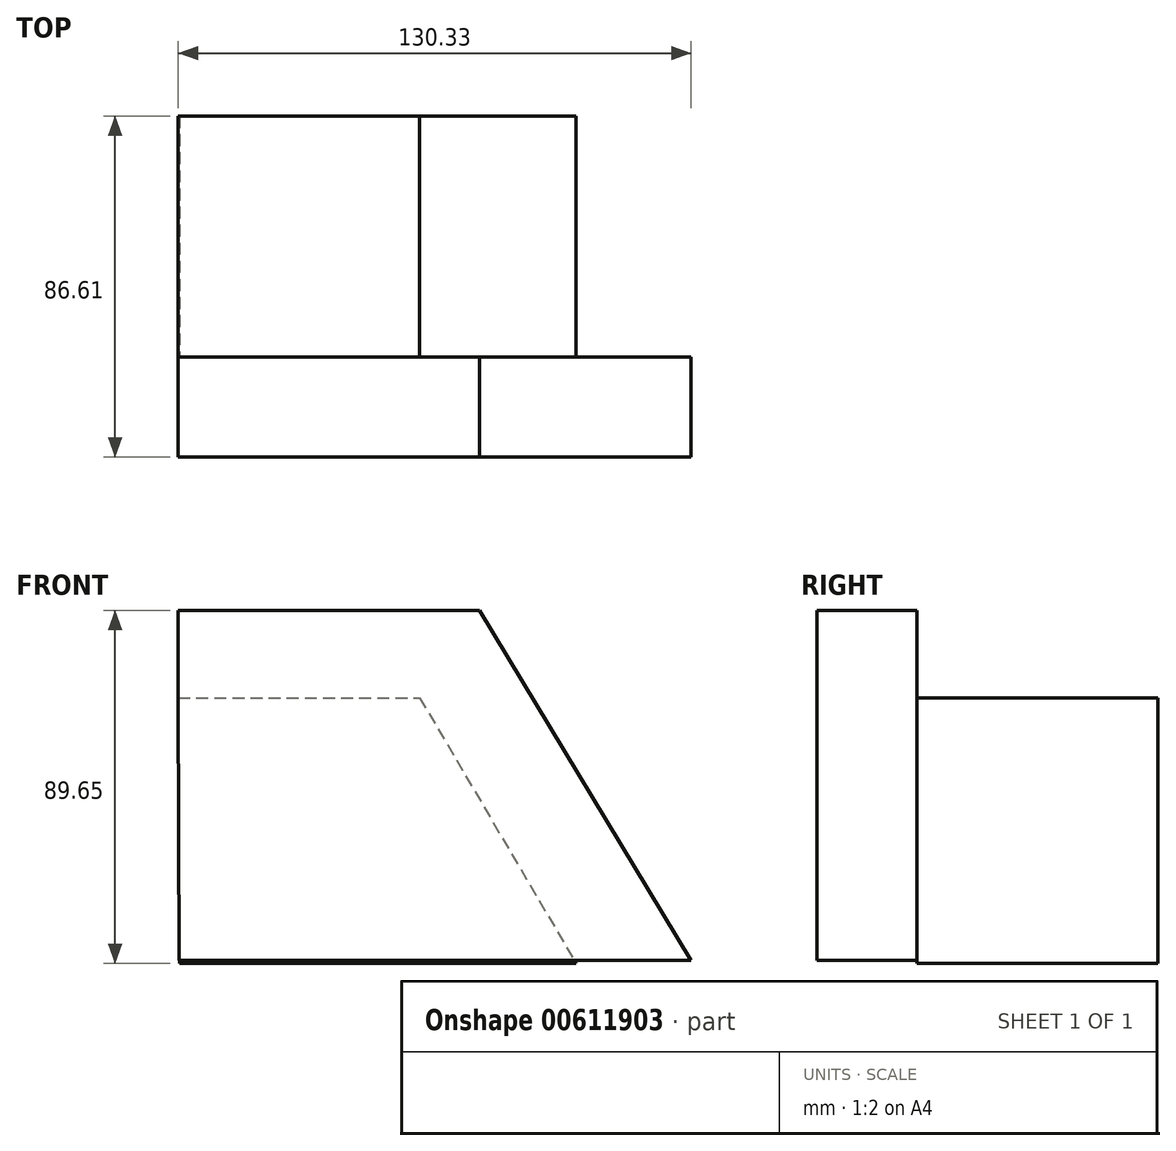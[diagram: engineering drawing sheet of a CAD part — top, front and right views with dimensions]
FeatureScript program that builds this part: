
annotation { "Feature Type Name" : "Feature", "Feature Type Description" : "" }
export const myFeature = defineFeature(function(context is Context, id is Id, definition is map)
    precondition{}
    {
        {
            var Q0;
            Q0=qCreatedBy(makeId("Front.planeOp"),FACE);
            var sketch = newSketch(context, id + "F0", { "sketchPlane" : qUnion([Q0])});
            skLineSegment(sketch, "E0", {"start": v(-76.5, 27.33) * mm, "end": v(-15.12, 27.33) * mm});
            skLineSegment(sketch, "E1", {"start": v(-15.12, 27.33) * mm, "end": v(24.58, -40.16) * mm});
            skLineSegment(sketch, "E2", {"start": v(24.58, -40.16) * mm, "end": v(-76.2, -40.16) * mm});
            skLineSegment(sketch, "E3", {"start": v(-76.2, -40.16) * mm, "end": v(-76.5, 27.33) * mm});
            skSolve(sketch);
        }
        {
            var Q0;
            Q0=makeQuery(id+"F0.imprint","IMPRINT",FACE,{"disambiguationData":[TD([[makeQuery(id+"F0.imprint","IMPRINT",EDGE,{"derivedFrom":sQuery(id+"F0.wireOp",EDGE,"E0")}),-1.0]])]});
            extrude(context, id + "F1", {"entities" : qUnion([Q0]), "oppositeDirection" : true, "depth" : 61.2 * mm, "offsetDistance" : 25.4 * mm});
        }
        {
            var Q0;
            Q0=qCreatedBy(makeId("Front.planeOp"),FACE);
            var sketch = newSketch(context, id + "F2", { "sketchPlane" : qUnion([Q0])});
            skLineSegment(sketch, "E4", {"start": v(-76.5, 27.31) * mm, "end": v(-76.5, 49.5) * mm});
            skLineSegment(sketch, "E5", {"start": v(-76.5, 49.5) * mm, "end": v(0, 49.5) * mm});
            skLineSegment(sketch, "E6", {"start": v(0, 49.5) * mm, "end": v(53.83, -39.4) * mm});
            skLineSegment(sketch, "E7", {"start": v(53.83, -39.4) * mm, "end": v(-76.3, -39.4) * mm});
            skLineSegment(sketch, "E8", {"start": v(-76.3, -39.4) * mm, "end": v(-76.5, 27.31) * mm});
            skSolve(sketch);
        }
        {
            var Q0;
            Q0=makeQuery(id+"F2.imprint","IMPRINT",FACE,{"disambiguationData":[TD([[makeQuery(id+"F2.imprint","IMPRINT",EDGE,{"derivedFrom":sQuery(id+"F2.wireOp",EDGE,"E4")}),-1.0]])]});
            extrude(context, id + "F3", {"entities" : qUnion([Q0]), "operationType" : NewBodyOperationType.ADD, "depth" : 25.4 * mm, "offsetDistance" : 25.4 * mm});
        }
    });
